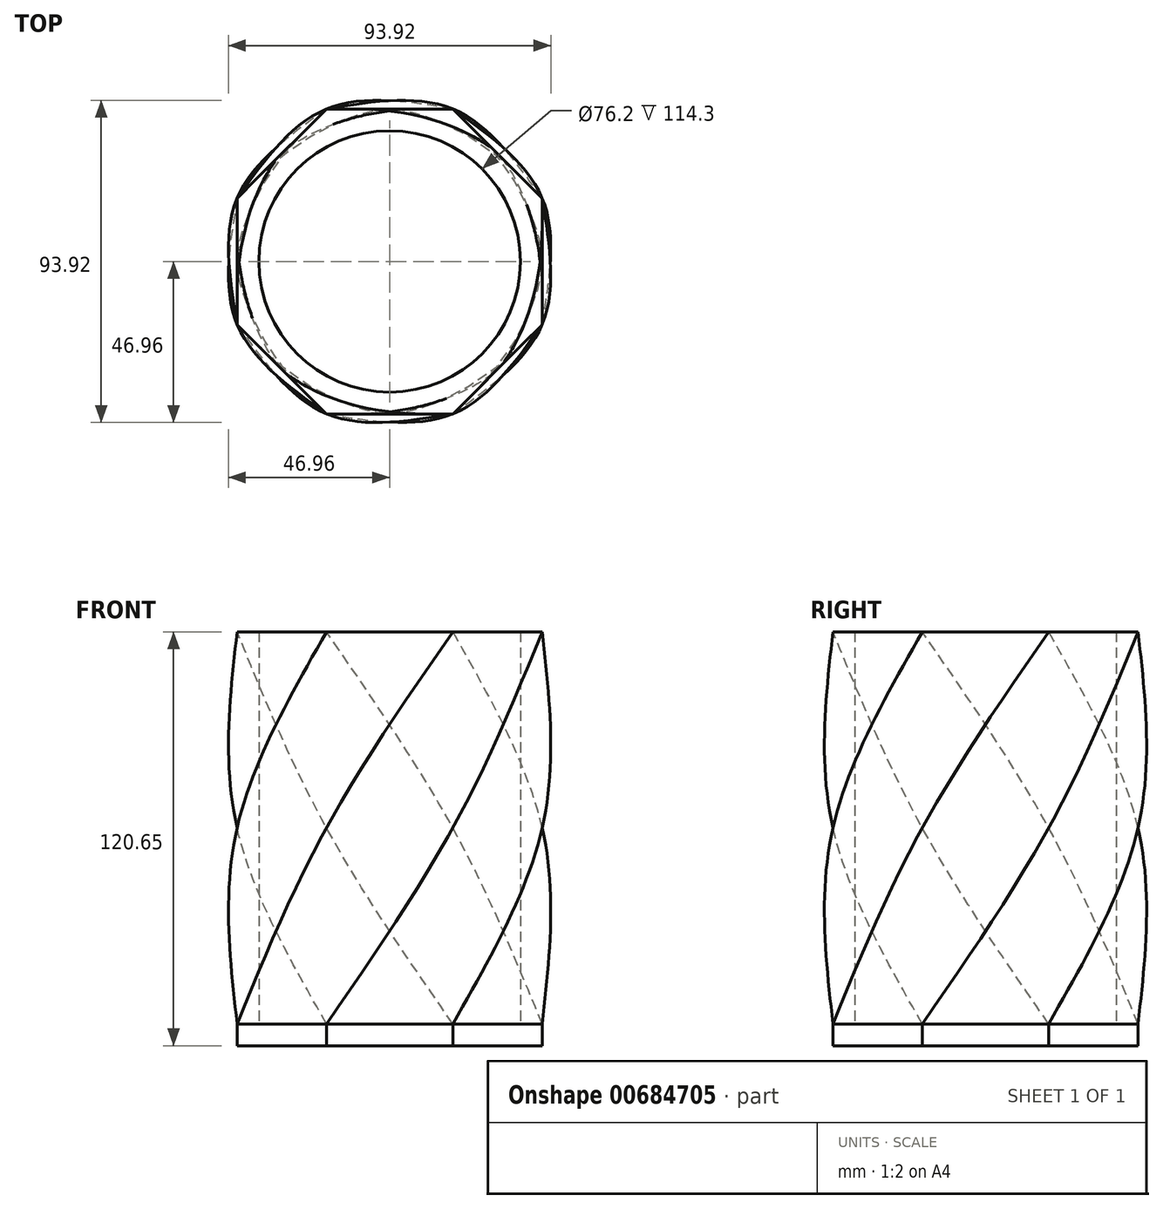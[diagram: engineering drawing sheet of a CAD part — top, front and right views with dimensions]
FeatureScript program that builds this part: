
annotation { "Feature Type Name" : "Feature", "Feature Type Description" : "" }
export const myFeature = defineFeature(function(context is Context, id is Id, definition is map)
    precondition{}
    {
        {
            var Q0;
            Q0=qCreatedBy(makeId("Top.planeOp"),FACE);
            var sketch = newSketch(context, id + "F0", { "sketchPlane" : qUnion([Q0])});
            skCircle(sketch, "E0", {"center": v(0, 0) * mm, "radius": 38.1 * mm});
            skCircle(sketch, "E1.cCircle", {"center": v(0, 0) * mm, "radius": 44.45 * mm, "construction": true});
            skLineSegment(sketch, "E1.0", {"start": v(-18.41, 44.45) * mm, "end": v(18.41, 44.45) * mm});
            skLineSegment(sketch, "E1.1", {"start": v(18.41, 44.45) * mm, "end": v(44.45, 18.41) * mm});
            skLineSegment(sketch, "E1.2", {"start": v(44.45, 18.41) * mm, "end": v(44.45, -18.41) * mm});
            skLineSegment(sketch, "E1.3", {"start": v(44.45, -18.41) * mm, "end": v(18.41, -44.45) * mm});
            skLineSegment(sketch, "E1.4", {"start": v(18.41, -44.45) * mm, "end": v(-18.41, -44.45) * mm});
            skLineSegment(sketch, "E1.5", {"start": v(-18.41, -44.45) * mm, "end": v(-44.45, -18.41) * mm});
            skLineSegment(sketch, "E1.6", {"start": v(-44.45, -18.41) * mm, "end": v(-44.45, 18.41) * mm});
            skLineSegment(sketch, "E1.7", {"start": v(-44.45, 18.41) * mm, "end": v(-18.41, 44.45) * mm});
            skPoint(sketch, "E1.0.midPoint", {"position": v(0, 44.45) * mm});
            skLineSegment(sketch, "E2", {"start": v(-38.1, 0) * mm, "end": v(0, 0) * mm});
            skLineSegment(sketch, "E3", {"start": v(-38.1, 0) * mm, "end": v(-44.45, 0) * mm, "construction": true});
            skLineSegment(sketch, "E4", {"start": v(0, 0) * mm, "end": v(0, 38.1) * mm});
            skLineSegment(sketch, "E5", {"start": v(0, 0) * mm, "end": v(38.1, 0) * mm});
            skSolve(sketch);
        }
        {
            var Q0;
            {var subQ0=sQuery(id+"F0.wireOp",EDGE,"E2");Q0=makeQuery(id+"F0.imprint","IMPRINT",FACE,{"disambiguationData":[TD([[makeQuery(id+"F0.imprint","IMPRINT",EDGE,{"derivedFrom":subQ0}),1.0]])]});}
            extrude(context, id + "F1", {"entities" : qUnion([Q0]), "depth" : 114.3 * mm, "offsetDistance" : 25.4 * mm});
        }
        {
            var Q0;
            Q0=qCreatedBy(makeId("Top.planeOp"),FACE);
            var sketch = newSketch(context, id + "F2", { "sketchPlane" : qUnion([Q0])});
            skCircle(sketch, "E6.cCircle", {"center": v(0, 0) * mm, "radius": 44.45 * mm, "construction": true});
            skLineSegment(sketch, "E6.0", {"start": v(-18.41, -44.45) * mm, "end": v(-44.45, -18.41) * mm});
            skLineSegment(sketch, "E6.1", {"start": v(-44.45, -18.41) * mm, "end": v(-44.45, 18.41) * mm});
            skLineSegment(sketch, "E6.2", {"start": v(-44.45, 18.41) * mm, "end": v(-18.41, 44.45) * mm});
            skLineSegment(sketch, "E6.3", {"start": v(-18.41, 44.45) * mm, "end": v(18.41, 44.45) * mm});
            skLineSegment(sketch, "E6.4", {"start": v(18.41, 44.45) * mm, "end": v(44.45, 18.41) * mm});
            skLineSegment(sketch, "E6.5", {"start": v(44.45, 18.41) * mm, "end": v(44.45, -18.41) * mm});
            skLineSegment(sketch, "E6.6", {"start": v(44.45, -18.41) * mm, "end": v(18.41, -44.45) * mm});
            skLineSegment(sketch, "E6.7", {"start": v(18.41, -44.45) * mm, "end": v(-18.41, -44.45) * mm});
            skPoint(sketch, "E6.0.midPoint", {"position": v(-31.43, -31.43) * mm});
            skSolve(sketch);
        }
        {
            var Q0;
            Q0=qCreatedBy(makeId("Front.planeOp"),FACE);
            var sketch = newSketch(context, id + "F3", { "sketchPlane" : qUnion([Q0])});
            skLineSegment(sketch, "E7.0", {"start": v(18.41, 0) * mm, "end": v(-18.41, 0) * mm});
            skLineSegment(sketch, "E8", {"start": v(18.41, 0) * mm, "end": v(18.41, 57.15) * mm});
            skLineSegment(sketch, "E9", {"start": v(18.41, 57.15) * mm, "end": v(18.41, 114.3) * mm});
            skLineSegment(sketch, "E10", {"start": v(18.41, 114.3) * mm, "end": v(-18.41, 0) * mm});
            skPoint(sketch, "E11.0", {"position": v(0, 114.3) * mm});
            skSolve(sketch);
        }
        {
            var Q0;
            Q0=sQuery(id+"F3.wireOp",VERTEX,"E10.start");
            var Q1;
            Q1=sQuery(id+"F3.wireOp",VERTEX,"E7.0.start");
            cPlane(context, id + "F4", {"entities" : qUnion([Q0, Q1]), "cplaneType" : CPlaneType.MID_PLANE, "offset" : 25.4 * mm, "width" : 152.4 * mm, "height" : 152.4 * mm});
        }
        {
            var Q0;
            Q0=sQuery(id+"F3.wireOp",VERTEX,"E10.start");
            var Q1;
            Q1=sQuery(id+"F3.wireOp",EDGE,"E9");
            cPlane(context, id + "F5", {"entities" : qUnion([Q0, Q1]), "cplaneType" : CPlaneType.LINE_POINT, "offset" : 25.4 * mm, "width" : 152.4 * mm, "height" : 152.4 * mm});
        }
        {
            var Q0;
            Q0=qCreatedBy(id+"F4.planeOp",FACE);
            var sketch = newSketch(context, id + "F6", { "sketchPlane" : qUnion([Q0])});
            skCircle(sketch, "E12.cCircle", {"center": v(0, 0) * mm, "radius": 44.45 * mm, "construction": true});
            skLineSegment(sketch, "E12.0", {"start": v(-18.41, -44.45) * mm, "end": v(-44.45, -18.41) * mm});
            skLineSegment(sketch, "E12.1", {"start": v(-44.45, -18.41) * mm, "end": v(-44.45, 18.41) * mm});
            skLineSegment(sketch, "E12.2", {"start": v(-44.45, 18.41) * mm, "end": v(-18.41, 44.45) * mm});
            skLineSegment(sketch, "E12.3", {"start": v(-18.41, 44.45) * mm, "end": v(18.41, 44.45) * mm});
            skLineSegment(sketch, "E12.4", {"start": v(18.41, 44.45) * mm, "end": v(44.45, 18.41) * mm});
            skLineSegment(sketch, "E12.5", {"start": v(44.45, 18.41) * mm, "end": v(44.45, -18.41) * mm});
            skLineSegment(sketch, "E12.6", {"start": v(44.45, -18.41) * mm, "end": v(18.41, -44.45) * mm});
            skLineSegment(sketch, "E12.7", {"start": v(18.41, -44.45) * mm, "end": v(-18.41, -44.45) * mm});
            skPoint(sketch, "E12.0.midPoint", {"position": v(-31.43, -31.43) * mm});
            skSolve(sketch);
        }
        {
            var Q0;
            Q0=qCreatedBy(id+"F5.planeOp",FACE);
            var sketch = newSketch(context, id + "F7", { "sketchPlane" : qUnion([Q0])});
            skCircle(sketch, "E13.cCircle", {"center": v(0, 0) * mm, "radius": 44.45 * mm, "construction": true});
            skLineSegment(sketch, "E13.0", {"start": v(-18.41, -44.45) * mm, "end": v(-44.45, -18.41) * mm});
            skLineSegment(sketch, "E13.1", {"start": v(-44.45, -18.41) * mm, "end": v(-44.45, 18.41) * mm});
            skLineSegment(sketch, "E13.2", {"start": v(-44.45, 18.41) * mm, "end": v(-18.41, 44.45) * mm});
            skLineSegment(sketch, "E13.3", {"start": v(-18.41, 44.45) * mm, "end": v(18.41, 44.45) * mm});
            skLineSegment(sketch, "E13.4", {"start": v(18.41, 44.45) * mm, "end": v(44.45, 18.41) * mm});
            skLineSegment(sketch, "E13.5", {"start": v(44.45, 18.41) * mm, "end": v(44.45, -18.41) * mm});
            skLineSegment(sketch, "E13.6", {"start": v(44.45, -18.41) * mm, "end": v(18.41, -44.45) * mm});
            skLineSegment(sketch, "E13.7", {"start": v(18.41, -44.45) * mm, "end": v(-18.41, -44.45) * mm});
            skPoint(sketch, "E13.0.midPoint", {"position": v(-31.43, -31.43) * mm});
            skSolve(sketch);
        }
        {
            var Q1;
            Q1=makeQuery(id+"F2.imprint","IMPRINT",FACE,{"disambiguationData":[TD([[makeQuery(id+"F2.imprint","IMPRINT",EDGE,{"derivedFrom":sQuery(id+"F2.wireOp",EDGE,"E6.0")}),-1.0]])]});
            var Q2;
            Q2=makeQuery(id+"F6.imprint","IMPRINT",FACE,{"disambiguationData":[TD([[makeQuery(id+"F6.imprint","IMPRINT",EDGE,{"derivedFrom":sQuery(id+"F6.wireOp",EDGE,"E12.0")}),-1.0]])]});
            var Q3;
            Q3=makeQuery(id+"F7.imprint","IMPRINT",FACE,{"disambiguationData":[TD([[makeQuery(id+"F7.imprint","IMPRINT",EDGE,{"derivedFrom":sQuery(id+"F7.wireOp",EDGE,"E13.0")}),-1.0]])]});
            var Q4;
            Q4=sQuery(id+"F2.wireOp",VERTEX,"E6.7.end");
            var Q5;
            Q5=sQuery(id+"F6.wireOp",VERTEX,"E12.4.start");
            var Q6;
            Q6=sQuery(id+"F7.wireOp",VERTEX,"E13.6.start");
            loft(context, id + "F8", {"sheetProfilesArray" : [{ "sheetProfileEntities" : qUnion([Q1]) }, { "sheetProfileEntities" : qUnion([Q2]) }, { "sheetProfileEntities" : qUnion([Q3]) }], "matchConnections" : true, "connections" : [{ "connectionEntities" : qUnion([Q4, Q5, Q6]), "connectionEdgeQueries" : qUnion([]), "connectionEdgeParameters" : [] }]});
        }
        {
            var Q0;
            Q0=makeQuery(id+"F1.opExtrude","SWEPT_BODY",BODY,{"disambiguationData":[OSD([sQuery(id+"F0.wireOp",EDGE,"E0"),sQuery(id+"F0.wireOp",EDGE,"E2"),sQuery(id+"F0.wireOp",EDGE,"E4")])]});
            deleteBodies(context, id + "F9", {"entities" : qUnion([Q0])});
        }
        {
            var Q0;
            Q0=qCreatedBy(makeId("Top.planeOp"),FACE);
            var sketch = newSketch(context, id + "F10", { "sketchPlane" : qUnion([Q0])});
            skCircle(sketch, "E14", {"center": v(0, 0) * mm, "radius": 38.1 * mm});
            skSolve(sketch);
        }
        {
            var Q0;
            Q0 = qSketchRegion(id + "F10", true);
            extrude(context, id + "F11", {"entities" : qUnion([Q0]), "operationType" : NewBodyOperationType.REMOVE, "depth" : 114.3 * mm, "offsetDistance" : 25.4 * mm});
        }
        {
            var Q0;
            Q0=makeQuery(id+"F2.imprint","IMPRINT",FACE,{"disambiguationData":[TD([[makeQuery(id+"F2.imprint","IMPRINT",EDGE,{"derivedFrom":sQuery(id+"F2.wireOp",EDGE,"E6.0")}),-1.0]])]});
            extrude(context, id + "F12", {"entities" : qUnion([Q0]), "operationType" : NewBodyOperationType.ADD, "oppositeDirection" : true, "depth" : 6.35 * mm, "offsetDistance" : 25.4 * mm});
        }
    });
